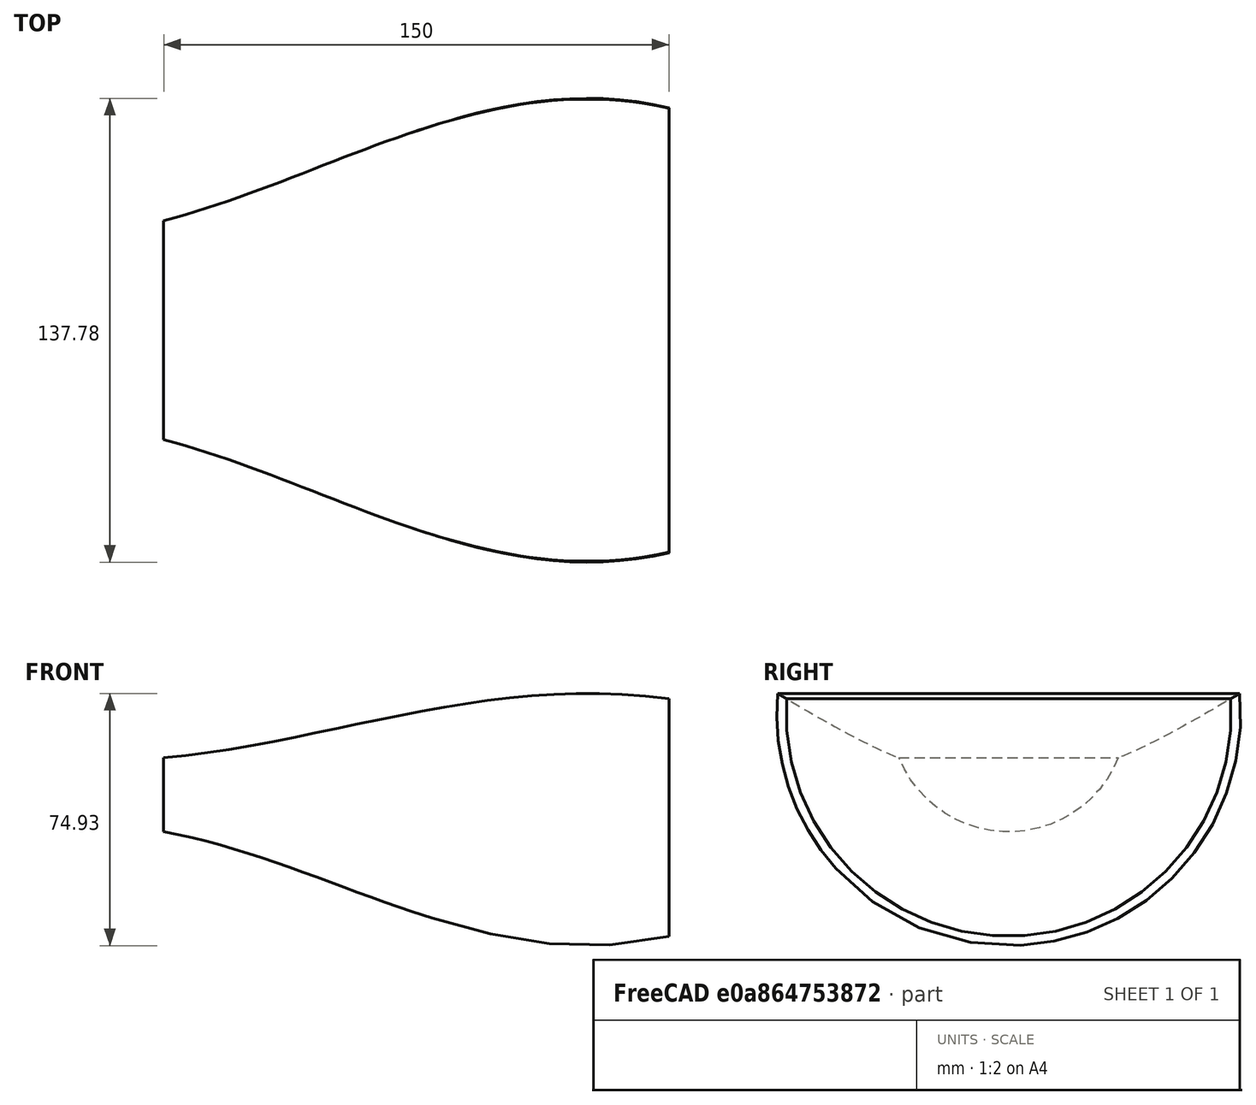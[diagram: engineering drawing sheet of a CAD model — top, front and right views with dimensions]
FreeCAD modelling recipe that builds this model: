
FCSTD DOCUMENT  (FreeCAD 0.20R29177 +426 (Git))
Label: project_10
License: All rights reserved
LicenseURL: https://en.wikipedia.org/wiki/All_rights_reserved
objects: Sketcher::SketchObject×5, Part::Loft×1
note: 6 computed .brp shape members not serialized (recipe doc carries the construction recipe); baked Part::Feature solids carry a one-line shape summary decoded from their .brp

FEATURE [Sketcher::SketchObject] Sketch
  FullyConstrained = false
  sketch-geometry (4):
    g0: LineSegment StartX=-100.243 StartY=0 StartZ=0 EndX=-50.2425 EndY=0 EndZ=0
    g1: LineSegment StartX=-50.2425 StartY=0 StartZ=0 EndX=-0.242542 EndY=0 EndZ=0
    g2: LineSegment StartX=-0.242542 StartY=0 StartZ=0 EndX=49.7575 EndY=0 EndZ=0
    g3: LineSegment StartX=49.7575 StartY=0 StartZ=0 EndX=99.7575 EndY=0 EndZ=0
  constraints (12):
    c: PointOnObject(g0,g-1)
    c: PointOnObject(g0,g-1)
    c: Coincident(g0,g1)
    c: PointOnObject(g1,g-1)
    c: Coincident(g1,g2)
    c: PointOnObject(g2,g-1)
    c: Coincident(g2,g3)
    c: PointOnObject(g3,g-1)
    c: DistanceX(g0,g0) = 50
    c: DistanceX(g1,g1) = 50
    c: DistanceX(g2,g2) = 50
    c: DistanceX(g3,g3) = 50
FEATURE [Sketcher::SketchObject] Sketch001
  FullyConstrained = false
  MapMode = 7
  Placement = pos=(49.7575,0,0) rot=(0.57735,-0.57735,-0.57735;2.0944rad)
  Support = -> [Sketch]
  sketch-geometry (2):
    g0: ArcOfCircle CenterX=0 CenterY=23.5961 CenterZ=0 NormalX=0 NormalY=0 NormalZ=1 AngleXU=0 Radius=66.0948 StartAngle=3.07477 EndAngle=6.35001
    g1: LineSegment StartX=-65.9473 StartY=28.0094 StartZ=0 EndX=65.9473 EndY=28.0094 EndZ=0
  constraints (4):
    c: PointOnObject(g0,g-2)
    c: Coincident(g1,g0)
    c: Coincident(g1,g0)
    c: Horizontal(g1)
FEATURE [Sketcher::SketchObject] Sketch002
  FullyConstrained = false
  MapMode = 7
  Placement = pos=(99.7575,0,0) rot=(0.57735,-0.57735,-0.57735;2.0944rad)
  Support = -> [Sketch]
  sketch-geometry (2):
    g0: ArcOfCircle CenterX=0 CenterY=23.5961 CenterZ=0 NormalX=0 NormalY=0 NormalZ=1 AngleXU=0 Radius=66.0948 StartAngle=3.07477 EndAngle=6.35001
    g1: LineSegment StartX=-65.9473 StartY=28.0094 StartZ=0 EndX=65.9473 EndY=28.0094 EndZ=0
  constraints (4):
    c: PointOnObject(g0,g-2)
    c: Coincident(g1,g0)
    c: Coincident(g1,g0)
    c: Horizontal(g1)
FEATURE [Sketcher::SketchObject] Sketch003
  FullyConstrained = false
  MapMode = 7
  Placement = pos=(-0.242542,0,0) rot=(0.57735,-0.57735,-0.57735;2.0944rad)
  Support = -> [Sketch]
  sketch-geometry (2):
    g0: ArcOfCircle CenterX=0 CenterY=23.5961 CenterZ=0 NormalX=0 NormalY=0 NormalZ=1 AngleXU=0 Radius=50.241 StartAngle=3.23479 EndAngle=6.18999
    g1: LineSegment StartX=-50.0229 StartY=18.9204 StartZ=0 EndX=50.0229 EndY=18.9204 EndZ=0
  constraints (4):
    c: PointOnObject(g0,g-2)
    c: Coincident(g1,g0)
    c: Coincident(g1,g0)
    c: Horizontal(g1)
FEATURE [Sketcher::SketchObject] Sketch004
  FullyConstrained = false
  MapMode = 7
  Placement = pos=(-50.2425,0,0) rot=(0.57735,-0.57735,-0.57735;2.0944rad)
  Support = -> [Sketch]
  sketch-geometry (2):
    g0: ArcOfCircle CenterX=0 CenterY=23.5961 CenterZ=0 NormalX=0 NormalY=0 NormalZ=1 AngleXU=0 Radius=35.0864 StartAngle=3.52465 EndAngle=5.90012
    g1: LineSegment StartX=-32.5435 StartY=10.4821 StartZ=0 EndX=32.5435 EndY=10.4821 EndZ=0
  constraints (4):
    c: PointOnObject(g0,g-2)
    c: Coincident(g1,g0)
    c: Coincident(g1,g0)
    c: Horizontal(g1)
FEATURE [Part::Loft] Loft
  Closed = false
  MaxDegree = 5
  Ruled = false
  Sections = -> [Sketch002,Sketch001,Sketch003,Sketch004]
  Solid = true
